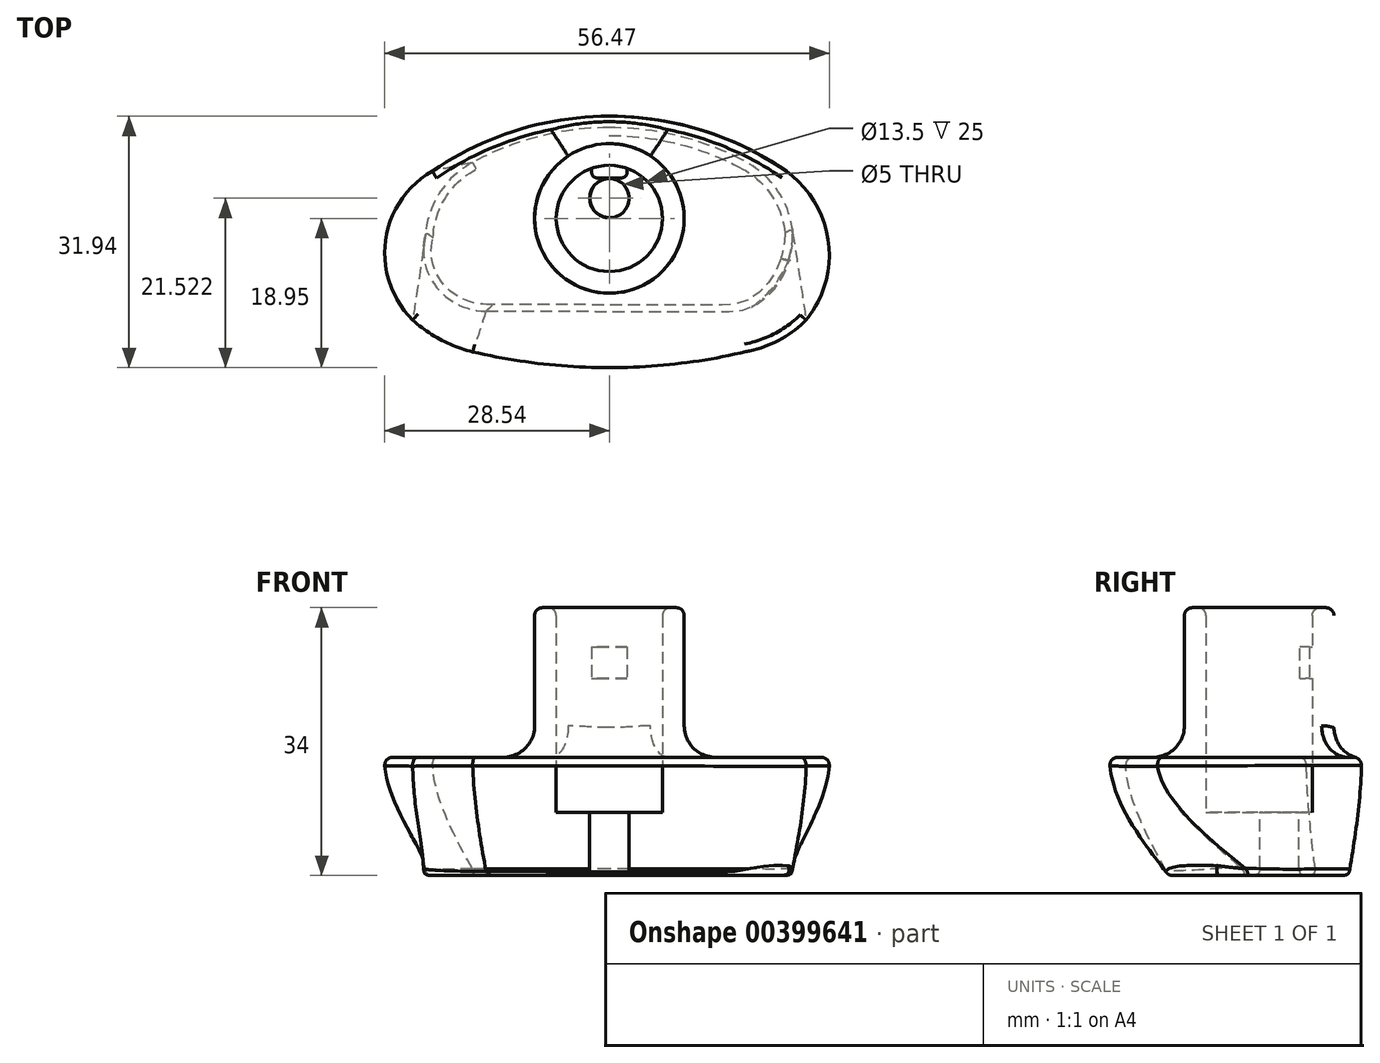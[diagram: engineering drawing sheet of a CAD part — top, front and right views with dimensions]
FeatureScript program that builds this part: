
annotation { "Feature Type Name" : "Feature", "Feature Type Description" : "" }
export const myFeature = defineFeature(function(context is Context, id is Id, definition is map)
    precondition{}
    {
        {
            var Q0;
            Q0=qCreatedBy(makeId("Top.planeOp"),FACE);
            var sketch = newSketch(context, id + "F0", { "sketchPlane" : qUnion([Q0])});
            skLineSegment(sketch, "E0.bottom", {"start": v(15.5, -11.5) * mm, "end": v(-15.58, -11.5) * mm});
            skPoint(sketch, "E0.middle", {"position": v(0, 0) * mm});
            skPoint(sketch, "E1.visualSharp", {"position": v(-23.5, 11.5) * mm});
            skPoint(sketch, "E2.visualSharp", {"position": v(23.5, 11.5) * mm});
            skPoint(sketch, "E3.visualSharp", {"position": v(-23.5, -11.5) * mm});
            skArc(sketch, "E3.filletArc", {"start": v(-23.22, -1.13) * mm, "mid": v(-22.02, -8.24) * mm, "end": v(-15.58, -11.5) * mm});
            skPoint(sketch, "E4.visualSharp", {"position": v(23.5, -11.5) * mm});
            skArc(sketch, "E4.filletArc", {"start": v(15.5, -11.5) * mm, "mid": v(21.1, -9.21) * mm, "end": v(23.5, -3.66) * mm});
            skPoint(sketch, "E5.visualSharp", {"position": v(-18.99, 6.99) * mm});
            skPoint(sketch, "E6.visualSharp", {"position": v(18.99, 6.99) * mm});
            skArc(sketch, "E6.filletArc", {"start": v(23.5, -3.66) * mm, "mid": v(23.39, -2.13) * mm, "end": v(23.1, -0.63) * mm});
            skArc(sketch, "E7", {"start": v(16.86, 7.3) * mm, "mid": v(-0.04, 11.4) * mm, "end": v(-16.92, 7.22) * mm});
            skPoint(sketch, "E8.visualSharp", {"position": v(-19.53, 5.71) * mm});
            skArc(sketch, "E8.filletArc", {"start": v(-16.92, 7.22) * mm, "mid": v(-21, 3.75) * mm, "end": v(-23.22, -1.13) * mm});
            skPoint(sketch, "E9.visualSharp", {"position": v(19.39, 5.86) * mm});
            skArc(sketch, "E9.filletArc", {"start": v(23.1, -0.63) * mm, "mid": v(20.84, 4) * mm, "end": v(16.86, 7.3) * mm});
            skSolve(sketch);
        }
        {
            var Q0;
            Q0=qCreatedBy(makeId("Top.planeOp"),FACE);
            cPlane(context, id + "F1", {"entities" : qUnion([Q0]), "cplaneType" : CPlaneType.OFFSET, "offset" : 15 * mm, "width" : 150 * mm, "height" : 150 * mm});
        }
        {
            var Q0;
            Q0=qCreatedBy(id+"F1.planeOp",FACE);
            var sketch = newSketch(context, id + "F2", { "sketchPlane" : qUnion([Q0])});
            skLineSegment(sketch, "E10.0.8", {"start": v(26, 0) * mm, "end": v(26, 0) * mm});
            skPoint(sketch, "E11", {"position": v(0, 0) * mm});
            skLineSegment(sketch, "E12", {"start": v(0, 0) * mm, "end": v(0, 13) * mm, "construction": true});
            skLineSegment(sketch, "E13", {"start": v(0, 0) * mm, "end": v(0, -19) * mm, "construction": true});
            skLineSegment(sketch, "E14", {"start": v(0, 0) * mm, "end": v(-26, 0) * mm, "construction": true});
            skLineSegment(sketch, "E15", {"start": v(0, 0) * mm, "end": v(26, 0) * mm, "construction": true});
            skLineSegment(sketch, "E16", {"start": v(-26, 0) * mm, "end": v(-26, 6) * mm, "construction": true});
            skLineSegment(sketch, "E17", {"start": v(26, 0) * mm, "end": v(26, 6) * mm, "construction": true});
            skLineSegment(sketch, "E18", {"start": v(-26, 6) * mm, "end": v(-22.5, 6) * mm, "construction": true});
            skLineSegment(sketch, "E19", {"start": v(26, 6) * mm, "end": v(22.5, 6) * mm, "construction": true});
            skArc(sketch, "E20", {"start": v(0, 13) * mm, "mid": v(-11.78, 11.2) * mm, "end": v(-22.5, 6) * mm});
            skArc(sketch, "E21", {"start": v(22.5, 6) * mm, "mid": v(11.78, 11.2) * mm, "end": v(0, 13) * mm});
            skLineSegment(sketch, "E22", {"start": v(-26, 0) * mm, "end": v(-26, -13) * mm, "construction": true});
            skLineSegment(sketch, "E23", {"start": v(26, 0) * mm, "end": v(26, -13) * mm, "construction": true});
            skLineSegment(sketch, "E24", {"start": v(-26, -13) * mm, "end": v(-25, -13) * mm, "construction": true});
            skLineSegment(sketch, "E25", {"start": v(26, -13) * mm, "end": v(25, -13) * mm, "construction": true});
            skLineSegment(sketch, "E26", {"start": v(0, -19) * mm, "end": v(-17.37, -19) * mm, "construction": true});
            skLineSegment(sketch, "E27", {"start": v(-17.37, -19) * mm, "end": v(-17.37, -17) * mm, "construction": true});
            skLineSegment(sketch, "E28", {"start": v(0, -19) * mm, "end": v(17.37, -19) * mm, "construction": true});
            skLineSegment(sketch, "E29", {"start": v(17.37, -19) * mm, "end": v(17.37, -17) * mm, "construction": true});
            skArc(sketch, "E30", {"start": v(0, -19) * mm, "mid": v(8.74, -18.5) * mm, "end": v(17.37, -17) * mm});
            skArc(sketch, "E31", {"start": v(-17.37, -17) * mm, "mid": v(-8.74, -18.5) * mm, "end": v(0, -19) * mm});
            skLineSegment(sketch, "E32", {"start": v(0, 13) * mm, "end": v(-21.2, 13) * mm, "construction": true});
            skArc(sketch, "E33", {"start": v(25, -13) * mm, "mid": v(27.86, -2.96) * mm, "end": v(22.5, 6) * mm});
            skArc(sketch, "E34", {"start": v(-22.5, 6) * mm, "mid": v(-28.49, -2.88) * mm, "end": v(-25, -13) * mm});
            skArc(sketch, "E35", {"start": v(-25, -13) * mm, "mid": v(-21.42, -15.44) * mm, "end": v(-17.37, -17) * mm});
            skArc(sketch, "E36", {"start": v(17.37, -17) * mm, "mid": v(21.5, -15.59) * mm, "end": v(25, -13) * mm});
            skSolve(sketch);
        }
        {
            var Q0;
            {var subQ5=sQuery(id+"F0.wireOp",EDGE,"E0.bottom");Q0=makeQuery(id+"F0.imprint","IMPRINT",FACE,{"disambiguationData":[TD([[makeQuery(id+"F0.imprint","IMPRINT",EDGE,{"derivedFrom":subQ5}),-1.0]])]});}
            var Q1;
            Q1=makeQuery(id+"F2.imprint","IMPRINT",FACE,{"disambiguationData":[TD([[makeQuery(id+"F2.imprint","IMPRINT",EDGE,{"derivedFrom":sQuery(id+"F2.wireOp",EDGE,"E20")}),1.0]])]});
            var Q2;
            Q2=sQuery(id+"F0.wireOp",EDGE,"E3.filletArc");
            var Q3;
            Q3=sQuery(id+"F2.wireOp",EDGE,"vF7bZy1M-c5l0-XUHJ-MQNS-8vcBr47cjl5g");
            var Q4;
            Q4=sQuery(id+"F2.wireOp",EDGE,"E34");
            var Q5;
            Q5=sQuery(id+"F0.wireOp",EDGE,"E8.filletArc");
            var Q6;
            Q6=sQuery(id+"F0.wireOp",EDGE,"E5.filletArc");
            var Q7;
            Q7=sQuery(id+"F0.wireOp",EDGE,"E4.filletArc");
            var Q8;
            Q8=sQuery(id+"F0.wireOp",EDGE,"E6.filletArc");
            var Q9;
            Q9=sQuery(id+"F0.wireOp",EDGE,"E9.filletArc");
            var Q10;
            Q10=sQuery(id+"F2.wireOp",EDGE,"FV8WmzPP-44fn-WbWa-2YER-E8hYZ5AOTLrY");
            var Q11;
            Q11=sQuery(id+"F2.wireOp",EDGE,"E33");
            var Q12;
            Q12=sQuery(id+"F2.wireOp",VERTEX,"E31.start");
            var Q13;
            Q13=sQuery(id+"F0.wireOp",VERTEX,"E3.filletArc.end");
            loft(context, id + "F3", {"startCondition" : LoftEndDerivativeType.NORMAL_TO_PROFILE, "startMagnitude" : 0, "endCondition" : LoftEndDerivativeType.NORMAL_TO_PROFILE, "endMagnitude" : 1, "sheetProfilesArray" : [{ "sheetProfileEntities" : qUnion([Q0]) }, { "sheetProfileEntities" : qUnion([Q1]) }], "guidesArray" : [{ "guideEntities" : qUnion([Q2]), "guideDerivativeType" : LoftGuideDerivativeType.DEFAULT, "guideDerivativeMagnitude" : 1 }, { "guideEntities" : qUnion([Q3]), "guideDerivativeType" : LoftGuideDerivativeType.DEFAULT, "guideDerivativeMagnitude" : 1 }, { "guideEntities" : qUnion([Q4]), "guideDerivativeType" : LoftGuideDerivativeType.DEFAULT, "guideDerivativeMagnitude" : 1 }, { "guideEntities" : qUnion([Q5]), "guideDerivativeType" : LoftGuideDerivativeType.DEFAULT, "guideDerivativeMagnitude" : 1 }, { "guideEntities" : qUnion([Q6]), "guideDerivativeType" : LoftGuideDerivativeType.DEFAULT, "guideDerivativeMagnitude" : 1 }, { "guideEntities" : qUnion([Q7]), "guideDerivativeType" : LoftGuideDerivativeType.DEFAULT, "guideDerivativeMagnitude" : 1 }, { "guideEntities" : qUnion([Q8]), "guideDerivativeType" : LoftGuideDerivativeType.DEFAULT, "guideDerivativeMagnitude" : 1 }, { "guideEntities" : qUnion([Q9]), "guideDerivativeType" : LoftGuideDerivativeType.DEFAULT, "guideDerivativeMagnitude" : 1 }, { "guideEntities" : qUnion([Q10]), "guideDerivativeType" : LoftGuideDerivativeType.DEFAULT, "guideDerivativeMagnitude" : 1 }, { "guideEntities" : qUnion([Q11]), "guideDerivativeType" : LoftGuideDerivativeType.DEFAULT, "guideDerivativeMagnitude" : 1 }], "matchConnections" : true, "connections" : [{ "connectionEntities" : qUnion([Q12, Q13]), "connectionEdgeQueries" : qUnion([]), "connectionEdgeParameters" : [] }]});
        }
        {
            var Q0;
            Q0=makeQuery(id+"F3.opLoft","CAP_FACE",FACE,{"disambiguationData":[OSD([makeQuery(id+"F2.imprint","IMPRINT",FACE,{"disambiguationData":[TD([[makeQuery(id+"F2.imprint","IMPRINT",EDGE,{"derivedFrom":sQuery(id+"F2.wireOp",EDGE,"E20")}),1.0]])]})])],"isStart":true});
            var sketch = newSketch(context, id + "F4", { "sketchPlane" : qUnion([Q0])});
            skCircle(sketch, "E37", {"center": v(0, 0) * mm, "radius": 9.5 * mm});
            skCircle(sketch, "E38", {"center": v(0, 0) * mm, "radius": 6.75 * mm});
            skSolve(sketch);
        }
        {
            var Q0;
            Q0 = qSketchRegion(id + "F4", true);
            extrude(context, id + "F5", {"entities" : qUnion([Q0]), "operationType" : NewBodyOperationType.ADD, "depth" : 19 * mm, "hasSecondDirection" : true, "secondDirectionOppositeDirection" : true, "secondDirectionDepth" : 9 * mm});
        }
        {
            var Q0;
            Q0=makeQuery(id+"F5.opExtrude","CAP_FACE",FACE,{"disambiguationData":[OSD([sQuery(id+"F4.wireOp",EDGE,"E37"),sQuery(id+"F4.wireOp",EDGE,"E38")])],"isStart":false});
            fillet(context, id + "F6", {"entities" : qUnion([Q0]), "radius" : 1 * mm, "tangentPropagation" : true, "allowEdgeOverflow" : false});
        }
        {
            var Q0;
            Q0=makeQuery(id+"F5.boolean.opBoolean","SPLIT",FACE,{"disambiguationData":[TD([makeQuery(id+"F5.opExtrude","SWEPT_FACE",FACE,{"disambiguationData":[OSD([sQuery(id+"F4.wireOp",EDGE,"E38")])]})])],"derivedFrom":makeQuery(id+"F3.opLoft","CAP_FACE",FACE,{"disambiguationData":[OSD([makeQuery(id+"F2.imprint","IMPRINT",FACE,{"disambiguationData":[TD([[makeQuery(id+"F2.imprint","IMPRINT",EDGE,{"derivedFrom":sQuery(id+"F2.wireOp",EDGE,"E20")}),1.0]])]})])],"isStart":true})});
            extrude(context, id + "F7", {"entities" : qUnion([Q0]), "operationType" : NewBodyOperationType.REMOVE, "oppositeDirection" : true, "depth" : 7 * mm});
        }
        {
            var Q0;
            Q0=makeQuery(id+"F7.boolean.opBoolean","COPY",FACE,{"derivedFrom":makeQuery(id+"F7.opExtrude","CAP_FACE",FACE,{"disambiguationData":[OSD([makeQuery(id+"F2.imprint","IMPRINT",FACE,{"disambiguationData":[TD([[makeQuery(id+"F2.imprint","IMPRINT",EDGE,{"derivedFrom":sQuery(id+"F2.wireOp",EDGE,"E20")}),1.0]])]})])],"isStart":false})});
            var sketch = newSketch(context, id + "F8", { "sketchPlane" : qUnion([Q0])});
            skCircle(sketch, "E39", {"center": v(0, 2.57) * mm, "radius": 2.5 * mm});
            skSolve(sketch);
        }
        {
            var Q0;
            Q0=makeQuery(id+"F8.imprint","IMPRINT",FACE,{"disambiguationData":[TD([[makeQuery(id+"F8.imprint","IMPRINT",EDGE,{"derivedFrom":sQuery(id+"F8.wireOp",EDGE,"E39")}),1.0]])]});
            extrude(context, id + "F9", {"entities" : qUnion([Q0]), "operationType" : NewBodyOperationType.REMOVE, "oppositeDirection" : true, "depth" : 25 * mm});
        }
        {
            var Q0;
            Q0=makeQuery(id+"F5.opExtrude","CAP_FACE",FACE,{"disambiguationData":[OSD([sQuery(id+"F4.wireOp",EDGE,"E37"),sQuery(id+"F4.wireOp",EDGE,"E38")])],"isStart":false});
            cPlane(context, id + "F10", {"entities" : qUnion([Q0]), "cplaneType" : CPlaneType.OFFSET, "offset" : 5 * mm, "oppositeDirection" : true, "width" : 150 * mm, "height" : 150 * mm});
        }
        {
            var Q0;
            Q0=qCreatedBy(id+"F10.planeOp",FACE);
            var sketch = newSketch(context, id + "F11", { "sketchPlane" : qUnion([Q0])});
            skLineSegment(sketch, "E40.bottom", {"start": v(-2.25, 7.15) * mm, "end": v(2.25, 7.15) * mm});
            skLineSegment(sketch, "E40.top", {"start": v(-1.55, 5.15) * mm, "end": v(1.55, 5.15) * mm});
            skLineSegment(sketch, "E40.left", {"start": v(-2.25, 7.15) * mm, "end": v(-2.25, 5.85) * mm});
            skLineSegment(sketch, "E40.right", {"start": v(2.25, 7.15) * mm, "end": v(2.25, 5.85) * mm});
            skLineSegment(sketch, "E41", {"start": v(0, 5.15) * mm, "end": v(0, 0) * mm, "construction": true});
            skPoint(sketch, "E41.startSnap0", {"position": v(0, 5.15) * mm});
            skPoint(sketch, "E42.visualSharp", {"position": v(-2.25, 5.15) * mm});
            skArc(sketch, "E42.filletArc", {"start": v(-2.25, 5.85) * mm, "mid": v(-2.04, 5.36) * mm, "end": v(-1.55, 5.15) * mm});
            skPoint(sketch, "E43.visualSharp", {"position": v(2.25, 5.15) * mm});
            skArc(sketch, "E43.filletArc", {"start": v(1.55, 5.15) * mm, "mid": v(2.04, 5.36) * mm, "end": v(2.25, 5.85) * mm});
            skSolve(sketch);
        }
        {
            var Q0;
            Q0 = qSketchRegion(id + "F11", true);
            extrude(context, id + "F12", {"entities" : qUnion([Q0]), "operationType" : NewBodyOperationType.ADD, "oppositeDirection" : true, "depth" : 4 * mm});
        }
        {
            var Q0;
            Q0=makeQuery(id+"F3.opLoft","MID_CAP_EDGE",EDGE,{"disambiguationData":[OSD([sQuery(id+"F2.wireOp",EDGE,"E30"),sQuery(id+"F2.wireOp",EDGE,"E31"),sQuery(id+"F2.wireOp",EDGE,"E35")])],"capPos":1.0});
            var Q1;
            Q1=makeQuery(id+"F3.opLoft","MID_CAP_EDGE",EDGE,{"disambiguationData":[OSD([sQuery(id+"F2.wireOp",EDGE,"E30"),sQuery(id+"F2.wireOp",EDGE,"E31"),sQuery(id+"F2.wireOp",EDGE,"E36")])],"capPos":1.0});
            var Q2;
            Q2=makeQuery(id+"F3.opLoft","MID_CAP_EDGE",EDGE,{"disambiguationData":[OSD([sQuery(id+"F2.wireOp",EDGE,"E30"),sQuery(id+"F2.wireOp",EDGE,"E33"),sQuery(id+"F2.wireOp",EDGE,"E36")])],"capPos":1.0});
            var Q3;
            Q3=makeQuery(id+"F3.opLoft","MID_CAP_EDGE",EDGE,{"disambiguationData":[OSD([sQuery(id+"F2.wireOp",EDGE,"E21"),sQuery(id+"F2.wireOp",EDGE,"E33"),sQuery(id+"F2.wireOp",EDGE,"E36")])],"capPos":1.0});
            var Q4;
            Q4=makeQuery(id+"F3.opLoft","MID_CAP_EDGE",EDGE,{"disambiguationData":[OSD([sQuery(id+"F2.wireOp",EDGE,"E20"),sQuery(id+"F2.wireOp",EDGE,"E21"),sQuery(id+"F2.wireOp",EDGE,"E33")])],"capPos":1.0});
            var Q5;
            Q5=makeQuery(id+"F3.opLoft","MID_CAP_EDGE",EDGE,{"disambiguationData":[OSD([sQuery(id+"F2.wireOp",EDGE,"E20"),sQuery(id+"F2.wireOp",EDGE,"E21"),sQuery(id+"F2.wireOp",EDGE,"E34")])],"capPos":1.0});
            var Q6;
            Q6=makeQuery(id+"F3.opLoft","MID_CAP_EDGE",EDGE,{"disambiguationData":[OSD([sQuery(id+"F2.wireOp",EDGE,"E20"),sQuery(id+"F2.wireOp",EDGE,"E34"),sQuery(id+"F2.wireOp",EDGE,"E35")])],"capPos":1.0});
            var Q7;
            Q7=makeQuery(id+"F3.opLoft","MID_CAP_EDGE",EDGE,{"disambiguationData":[OSD([sQuery(id+"F2.wireOp",EDGE,"E31"),sQuery(id+"F2.wireOp",EDGE,"E34"),sQuery(id+"F2.wireOp",EDGE,"E35")])],"capPos":1.0});
            fillet(context, id + "F13", {"entities" : qUnion([Q0, Q1, Q2, Q3, Q4, Q5, Q6, Q7]), "radius" : 1 * mm, "tangentPropagation" : true, "rho" : .4, "crossSection" : FilletCrossSection.CONIC, "allowEdgeOverflow" : false});
        }
        {
            var Q0;
            Q0=makeQuery(id+"F3.opLoft","CAP_FACE",FACE,{"disambiguationData":[OSD([makeQuery(id+"F0.imprint","IMPRINT",FACE,{"disambiguationData":[TD([[makeQuery(id+"F0.imprint","IMPRINT",EDGE,{"derivedFrom":sQuery(id+"F0.wireOp",EDGE,"E0.bottom")}),-1.0]])]})])],"isStart":true});
            fillet(context, id + "F14", {"entities" : qUnion([Q0]), "radius" : 1 * mm, "tangentPropagation" : true, "rho" : 0.6, "crossSection" : FilletCrossSection.CONIC, "allowEdgeOverflow" : false});
        }
        {
            var Q0;
            Q0=makeQuery(id+"F5.boolean.opBoolean","INTERSECT",EDGE,{"derivedFrom":[makeQuery(id+"F3.opLoft","CAP_FACE",FACE,{"disambiguationData":[OSD([makeQuery(id+"F2.imprint","IMPRINT",FACE,{"disambiguationData":[TD([[makeQuery(id+"F2.imprint","IMPRINT",EDGE,{"derivedFrom":sQuery(id+"F2.wireOp",EDGE,"E20")}),1.0]])]})])],"isStart":true}),makeQuery(id+"F5.opExtrude","SWEPT_FACE",FACE,{"disambiguationData":[OSD([sQuery(id+"F4.wireOp",EDGE,"E37")])]})]});
            fillet(context, id + "F15", {"entities" : qUnion([Q0]), "radius" : 4 * mm, "tangentPropagation" : true, "allowEdgeOverflow" : false});
        }
    });
